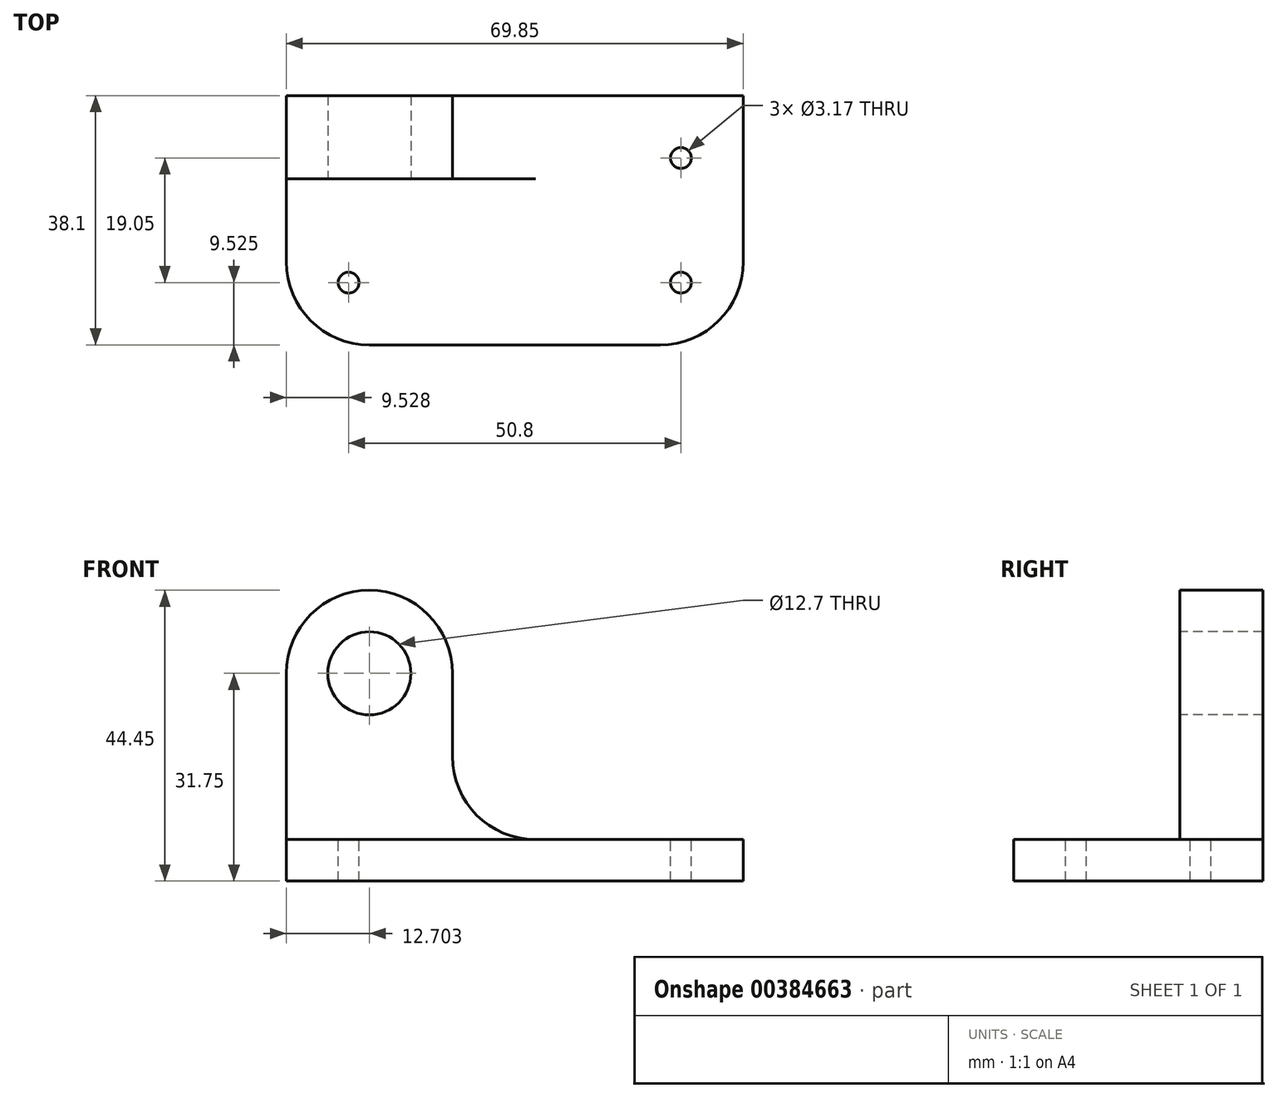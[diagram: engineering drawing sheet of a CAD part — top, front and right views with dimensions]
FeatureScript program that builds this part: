
annotation { "Feature Type Name" : "Feature", "Feature Type Description" : "" }
export const myFeature = defineFeature(function(context is Context, id is Id, definition is map)
    precondition{}
    {
        {
            var Q0;
            Q0=qCreatedBy(makeId("Front.planeOp"),FACE);
            var sketch = newSketch(context, id + "F0", { "sketchPlane" : qUnion([Q0])});
            skLineSegment(sketch, "E0", {"start": v(-42.86, 44.45) * mm, "end": v(-42.86, 0) * mm});
            skLineSegment(sketch, "E1", {"start": v(-42.86, 0) * mm, "end": v(27, 0) * mm});
            skLineSegment(sketch, "E2", {"start": v(-42.86, 44.45) * mm, "end": v(-17.46, 44.45) * mm});
            skLineSegment(sketch, "E3", {"start": v(-17.46, 44.45) * mm, "end": v(-17.46, 6.35) * mm});
            skLineSegment(sketch, "E4", {"start": v(-17.46, 6.35) * mm, "end": v(27, 6.35) * mm});
            skLineSegment(sketch, "E5", {"start": v(27, 6.35) * mm, "end": v(27, 0) * mm});
            skSolve(sketch);
        }
        {
            var Q0;
            Q0=makeQuery(id+"F0.imprint","IMPRINT",FACE,{"disambiguationData":[TD([[makeQuery(id+"F0.imprint","IMPRINT",EDGE,{"derivedFrom":sQuery(id+"F0.wireOp",EDGE,"E0")}),1.0]])]});
            extrude(context, id + "F1", {"entities" : qUnion([Q0]), "depth" : 38.1 * mm});
        }
        {
            var Q0;
            Q0=makeQuery(id+"F1.opExtrude","CAP_FACE",FACE,{"disambiguationData":[OSD([sQuery(id+"F0.wireOp",EDGE,"E0"),sQuery(id+"F0.wireOp",EDGE,"E1"),sQuery(id+"F0.wireOp",EDGE,"E2"),sQuery(id+"F0.wireOp",EDGE,"E3"),sQuery(id+"F0.wireOp",EDGE,"E4"),sQuery(id+"F0.wireOp",EDGE,"E5")])],"isStart":false});
            var sketch = newSketch(context, id + "F2", { "sketchPlane" : qUnion([Q0])});
            skLineSegment(sketch, "E6", {"start": v(-17.46, 6.35) * mm, "end": v(-42.86, 6.35) * mm});
            skLineSegment(sketch, "E7", {"start": v(-42.86, 6.35) * mm, "end": v(-42.86, 44.45) * mm});
            skLineSegment(sketch, "E8", {"start": v(-42.86, 44.45) * mm, "end": v(-17.46, 44.45) * mm});
            skLineSegment(sketch, "E9", {"start": v(-17.46, 44.45) * mm, "end": v(-17.46, 6.35) * mm});
            skSolve(sketch);
        }
        {
            var Q0;
            Q0=makeQuery(id+"F2.imprint","IMPRINT",FACE,{"disambiguationData":[TD([[makeQuery(id+"F2.imprint","IMPRINT",EDGE,{"derivedFrom":sQuery(id+"F2.wireOp",EDGE,"E6")}),-1.0]])]});
            extrude(context, id + "F3", {"entities" : qUnion([Q0]), "operationType" : NewBodyOperationType.REMOVE, "oppositeDirection" : true, "depth" : 25.4 * mm});
        }
        {
            var Q0;
            Q0=makeQuery(id+"F3.boolean.opBoolean","COPY",FACE,{"derivedFrom":makeQuery(id+"F3.opExtrude","CAP_FACE",FACE,{"disambiguationData":[OSD([sQuery(id+"F2.wireOp",EDGE,"E6"),sQuery(id+"F2.wireOp",EDGE,"E7"),sQuery(id+"F2.wireOp",EDGE,"E8"),sQuery(id+"F2.wireOp",EDGE,"E9")])],"isStart":false})});
            var sketch = newSketch(context, id + "F4", { "sketchPlane" : qUnion([Q0])});
            skCircle(sketch, "E10", {"center": v(-30.16, 31.75) * mm, "radius": 6.35 * mm});
            skSolve(sketch);
        }
        {
            var Q0;
            Q0=makeQuery(id+"F4.imprint","IMPRINT",FACE,{"disambiguationData":[TD([[makeQuery(id+"F4.imprint","IMPRINT",EDGE,{"derivedFrom":sQuery(id+"F4.wireOp",EDGE,"E10")}),1.0]])]});
            extrude(context, id + "F5", {"entities" : qUnion([Q0]), "operationType" : NewBodyOperationType.REMOVE, "oppositeDirection" : true, "depth" : 12.7 * mm});
        }
        {
            var Q0;
            Q0=makeQuery(id+"F3.boolean.opBoolean","COPY",FACE,{"derivedFrom":makeQuery(id+"F3.opExtrude","CAP_FACE",FACE,{"disambiguationData":[OSD([sQuery(id+"F2.wireOp",EDGE,"E6"),sQuery(id+"F2.wireOp",EDGE,"E7"),sQuery(id+"F2.wireOp",EDGE,"E8"),sQuery(id+"F2.wireOp",EDGE,"E9")])],"isStart":false})});
            var sketch = newSketch(context, id + "F6", { "sketchPlane" : qUnion([Q0])});
            skArc(sketch, "E11", {"start": v(-30.16, 44.45) * mm, "mid": v(-39.14, 40.73) * mm, "end": v(-42.86, 31.75) * mm});
            skArc(sketch, "E12", {"start": v(-17.46, 31.75) * mm, "mid": v(-21.18, 40.73) * mm, "end": v(-30.16, 44.45) * mm});
            skSolve(sketch);
        }
        {
            var Q0;
            {var subQ0=sQuery(id+"F6.wireOp",EDGE,"E11");Q0=makeQuery(id+"F6.imprint","IMPRINT",FACE,{"disambiguationData":[TD([[makeQuery(id+"F6.imprint","IMPRINT",EDGE,{"derivedFrom":subQ0}),-1.0]])]});}
            var Q1;
            {var subQ0=sQuery(id+"F6.wireOp",EDGE,"E12");Q1=makeQuery(id+"F6.imprint","IMPRINT",FACE,{"disambiguationData":[TD([[makeQuery(id+"F6.imprint","IMPRINT",EDGE,{"derivedFrom":subQ0}),-1.0]])]});}
            extrude(context, id + "F7", {"entities" : qUnion([Q0, Q1]), "operationType" : NewBodyOperationType.REMOVE, "oppositeDirection" : true, "depth" : 12.7 * mm});
        }
        {
            var Q0;
            Q0=makeQuery(id+"F3.boolean.opBoolean","COPY",FACE,{"derivedFrom":makeQuery(id+"F3.opExtrude","CAP_FACE",FACE,{"disambiguationData":[OSD([sQuery(id+"F2.wireOp",EDGE,"E6"),sQuery(id+"F2.wireOp",EDGE,"E7"),sQuery(id+"F2.wireOp",EDGE,"E8"),sQuery(id+"F2.wireOp",EDGE,"E9")])],"isStart":false})});
            var sketch = newSketch(context, id + "F8", { "sketchPlane" : qUnion([Q0])});
            skLineSegment(sketch, "E13", {"start": v(-17.46, 19.05) * mm, "end": v(-17.46, 6.35) * mm});
            skLineSegment(sketch, "E14", {"start": v(-17.46, 6.35) * mm, "end": v(-4.76, 6.35) * mm});
            skLineSegment(sketch, "E15", {"start": v(-17.46, 19.05) * mm, "end": v(-4.76, 19.05) * mm});
            skLineSegment(sketch, "E16", {"start": v(-4.76, 19.05) * mm, "end": v(-4.76, 6.35) * mm});
            skSolve(sketch);
        }
        {
            var Q0;
            Q0=makeQuery(id+"F8.imprint","IMPRINT",FACE,{"disambiguationData":[TD([[makeQuery(id+"F8.imprint","IMPRINT",EDGE,{"derivedFrom":sQuery(id+"F8.wireOp",EDGE,"E13")}),1.0]])]});
            extrude(context, id + "F9", {"entities" : qUnion([Q0]), "operationType" : NewBodyOperationType.ADD, "oppositeDirection" : true, "depth" : 12.7 * mm});
        }
        {
            var Q0;
            Q0=makeQuery(id+"F9.boolean.opBoolean","MERGE",FACE,{"derivedFrom":[makeQuery(id+"F3.boolean.opBoolean","COPY",FACE,{"derivedFrom":makeQuery(id+"F3.opExtrude","CAP_FACE",FACE,{"disambiguationData":[OSD([sQuery(id+"F2.wireOp",EDGE,"E6"),sQuery(id+"F2.wireOp",EDGE,"E7"),sQuery(id+"F2.wireOp",EDGE,"E8"),sQuery(id+"F2.wireOp",EDGE,"E9")])],"isStart":false})}),makeQuery(id+"F9.opExtrude","CAP_FACE",FACE,{"disambiguationData":[OSD([sQuery(id+"F8.wireOp",EDGE,"E13"),sQuery(id+"F8.wireOp",EDGE,"E14"),sQuery(id+"F8.wireOp",EDGE,"E15"),sQuery(id+"F8.wireOp",EDGE,"E16")])],"isStart":true})]});
            var sketch = newSketch(context, id + "F10", { "sketchPlane" : qUnion([Q0])});
            skArc(sketch, "E17", {"start": v(-17.46, 19.05) * mm, "mid": v(-13.74, 10.07) * mm, "end": v(-4.76, 6.35) * mm});
            skSolve(sketch);
        }
        {
            var Q0;
            Q0=makeQuery(id+"F10.imprint","IMPRINT",FACE,{"disambiguationData":[TD([[makeQuery(id+"F10.imprint","IMPRINT",EDGE,{"derivedFrom":sQuery(id+"F10.wireOp",EDGE,"E17")}),1.0]])]});
            extrude(context, id + "F11", {"entities" : qUnion([Q0]), "operationType" : NewBodyOperationType.REMOVE, "oppositeDirection" : true, "depth" : 12.7 * mm});
        }
        {
            var Q0;
            Q0=makeQuery(id+"F3.boolean.opBoolean","MERGE",FACE,{"derivedFrom":[makeQuery(id+"F1.opExtrude","SWEPT_FACE",FACE,{"disambiguationData":[OSD([sQuery(id+"F0.wireOp",EDGE,"E4")])]}),makeQuery(id+"F3.opExtrude","SWEPT_FACE",FACE,{"disambiguationData":[OSD([sQuery(id+"F2.wireOp",EDGE,"E6")])]})]});
            var sketch = newSketch(context, id + "F12", { "sketchPlane" : qUnion([Q0])});
            skCircle(sketch, "E18", {"center": v(-33.33, -28.57) * mm, "radius": 1.59 * mm});
            skCircle(sketch, "E19", {"center": v(17.47, -9.52) * mm, "radius": 1.59 * mm});
            skCircle(sketch, "E20", {"center": v(17.47, -28.58) * mm, "radius": 1.59 * mm});
            skSolve(sketch);
        }
        {
            var Q0;
            Q0=makeQuery(id+"F12.imprint","IMPRINT",FACE,{"disambiguationData":[TD([[makeQuery(id+"F12.imprint","IMPRINT",EDGE,{"derivedFrom":sQuery(id+"F12.wireOp",EDGE,"E18")}),1.0]])]});
            var Q1;
            Q1=makeQuery(id+"F12.imprint","IMPRINT",FACE,{"disambiguationData":[TD([[makeQuery(id+"F12.imprint","IMPRINT",EDGE,{"derivedFrom":sQuery(id+"F12.wireOp",EDGE,"E20")}),1.0]])]});
            var Q2;
            Q2=makeQuery(id+"F12.imprint","IMPRINT",FACE,{"disambiguationData":[TD([[makeQuery(id+"F12.imprint","IMPRINT",EDGE,{"derivedFrom":sQuery(id+"F12.wireOp",EDGE,"E19")}),1.0]])]});
            extrude(context, id + "F13", {"entities" : qUnion([Q0, Q1, Q2]), "operationType" : NewBodyOperationType.REMOVE, "oppositeDirection" : true, "depth" : 6.35 * mm});
        }
        {
            var Q0;
            Q0=makeQuery(id+"F3.boolean.opBoolean","MERGE",FACE,{"derivedFrom":[makeQuery(id+"F1.opExtrude","SWEPT_FACE",FACE,{"disambiguationData":[OSD([sQuery(id+"F0.wireOp",EDGE,"E4")])]}),makeQuery(id+"F3.opExtrude","SWEPT_FACE",FACE,{"disambiguationData":[OSD([sQuery(id+"F2.wireOp",EDGE,"E6")])]})]});
            var sketch = newSketch(context, id + "F14", { "sketchPlane" : qUnion([Q0])});
            skArc(sketch, "E21", {"start": v(-42.86, -25.4) * mm, "mid": v(-39.14, -34.38) * mm, "end": v(-30.16, -38.1) * mm});
            skArc(sketch, "E22", {"start": v(14.3, -38.1) * mm, "mid": v(23.27, -34.38) * mm, "end": v(27, -25.4) * mm});
            skSolve(sketch);
        }
        {
            var Q0;
            {var subQ0=sQuery(id+"F14.wireOp",EDGE,"E21");Q0=makeQuery(id+"F14.imprint","IMPRINT",FACE,{"disambiguationData":[TD([[makeQuery(id+"F14.imprint","IMPRINT",EDGE,{"derivedFrom":subQ0}),-1.0]])]});}
            var Q1;
            {var subQ0=sQuery(id+"F14.wireOp",EDGE,"E22");Q1=makeQuery(id+"F14.imprint","IMPRINT",FACE,{"disambiguationData":[TD([[makeQuery(id+"F14.imprint","IMPRINT",EDGE,{"derivedFrom":subQ0}),-1.0]])]});}
            extrude(context, id + "F15", {"entities" : qUnion([Q0, Q1]), "operationType" : NewBodyOperationType.REMOVE, "oppositeDirection" : true, "depth" : 6.35 * mm});
        }
    });
